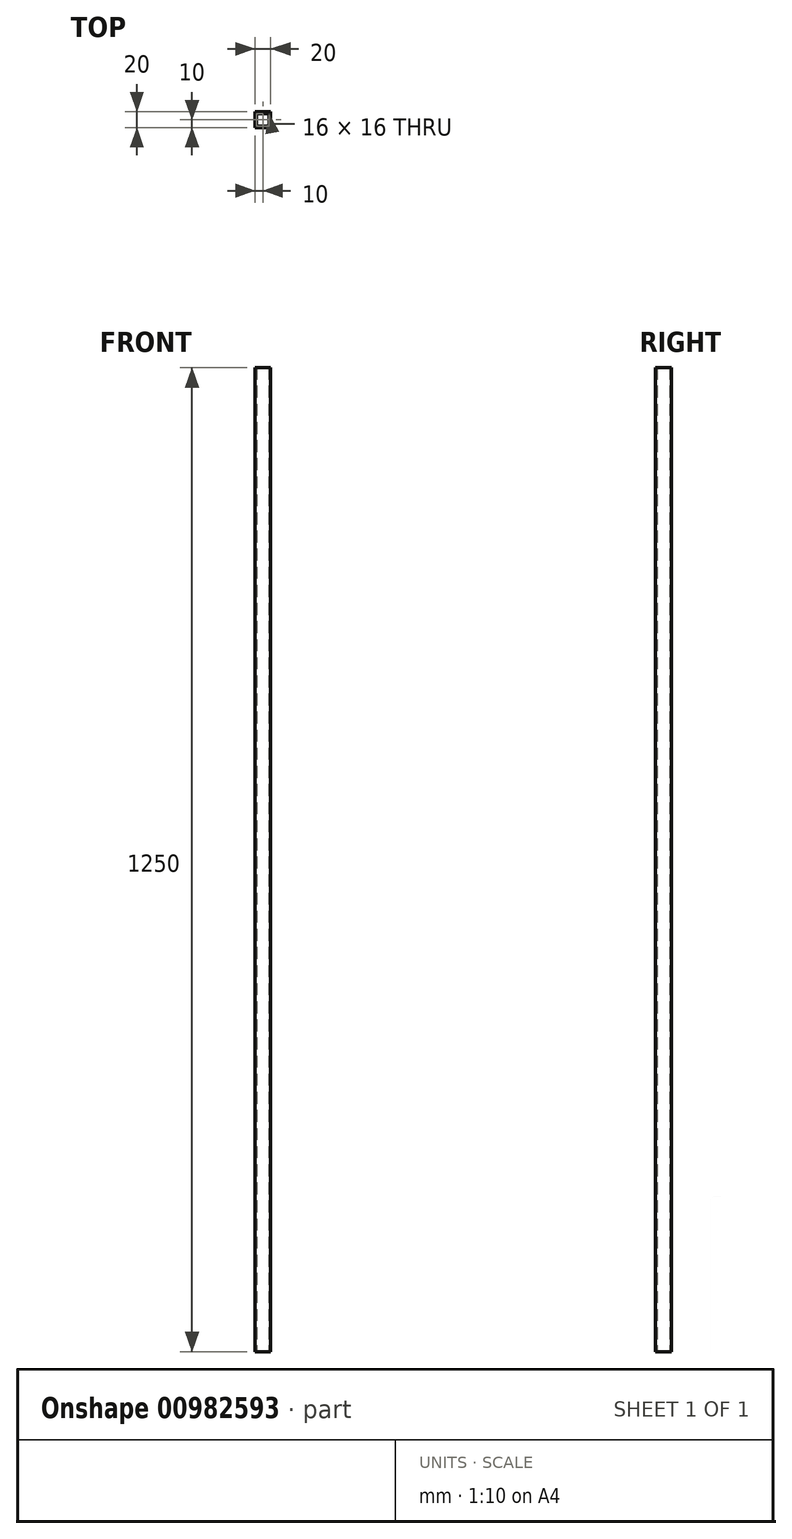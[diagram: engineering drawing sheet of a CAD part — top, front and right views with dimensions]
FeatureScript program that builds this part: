
annotation { "Feature Type Name" : "Feature", "Feature Type Description" : "" }
export const myFeature = defineFeature(function(context is Context, id is Id, definition is map)
    precondition{}
    {
        {
            var Q0;
            Q0=qCreatedBy(makeId("Top.planeOp"),FACE);
            var sketch = newSketch(context, id + "F0", { "sketchPlane" : qUnion([Q0])});
            skLineSegment(sketch, "E0.bottom", {"start": v(10, 10) * mm, "end": v(-10, 10) * mm});
            skLineSegment(sketch, "E0.top", {"start": v(10, -10) * mm, "end": v(-10, -10) * mm});
            skLineSegment(sketch, "E0.left", {"start": v(10, 10) * mm, "end": v(10, -10) * mm});
            skLineSegment(sketch, "E0.right", {"start": v(-10, 10) * mm, "end": v(-10, -10) * mm});
            skPoint(sketch, "E0.middle", {"position": v(0, 0) * mm});
            skLineSegment(sketch, "E1.bottom", {"start": v(8, -8) * mm, "end": v(-8, -8) * mm});
            skLineSegment(sketch, "E1.top", {"start": v(8, 8) * mm, "end": v(-8, 8) * mm});
            skLineSegment(sketch, "E1.left", {"start": v(8, -8) * mm, "end": v(8, 8) * mm});
            skLineSegment(sketch, "E1.right", {"start": v(-8, -8) * mm, "end": v(-8, 8) * mm});
            skSolve(sketch);
        }
        {
            var Q0;
            Q0=makeQuery(id+"F0.imprint","IMPRINT",FACE,{"disambiguationData":[TD([[makeQuery(id+"F0.imprint","IMPRINT",EDGE,{"derivedFrom":sQuery(id+"F0.wireOp",EDGE,"E0.bottom")}),1.0]])]});
            extrude(context, id + "F1", {"entities" : qUnion([Q0]), "depth" : 1250 * mm, "offsetDistance" : 25 * mm});
        }
    });
